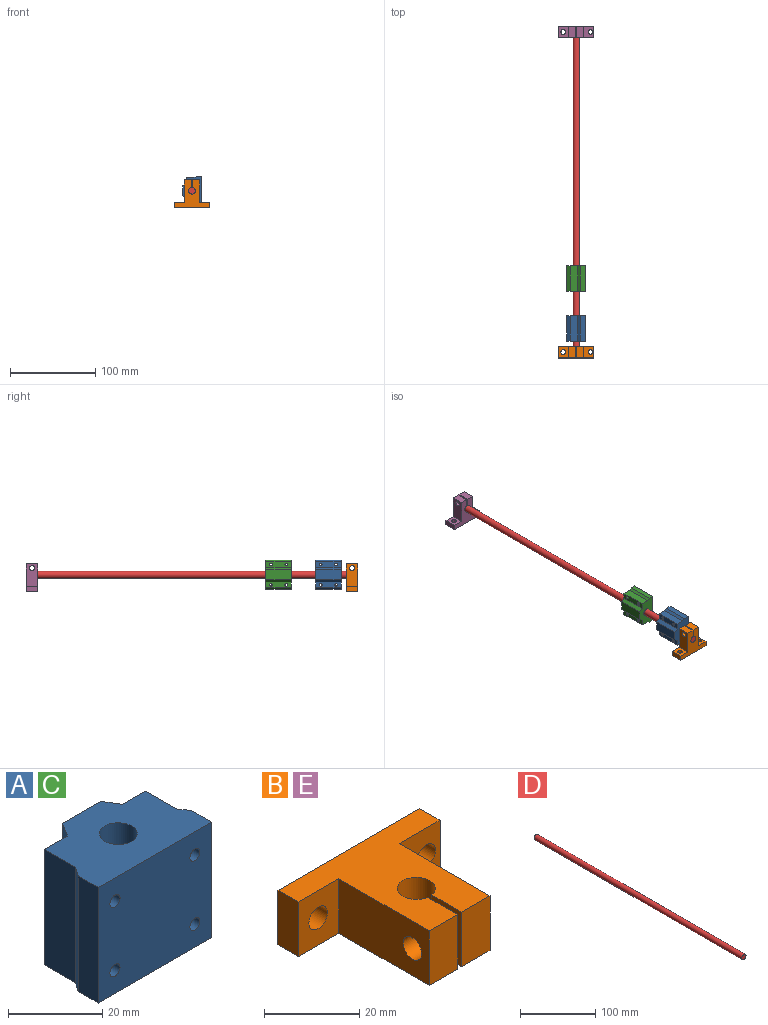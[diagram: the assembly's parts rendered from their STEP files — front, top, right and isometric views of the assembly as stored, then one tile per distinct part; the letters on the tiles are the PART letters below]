
ASSEMBLY  parts=5 mates=4
PART A: 19 faces, bbox 34x22x30 mm
  f0: plane 34x30mm, normal (0,-1,0), area 991mm2, adj f1,f12,f13,f14,f15,f16,f17,f18
  f1: plane 30x6mm, normal (-1,0,0), area 180mm2, adj f0,f2,f13,f14
  f2: plane 30x2.67mm, normal (-0.82,0.57,0), area 97.1mm2, adj f1,f3,f13,f14
  f3: plane 30x9.33mm, normal (-1,0,0), area 280mm2, adj f2,f4,f13,f14
  f4: plane 30x6.93mm, normal (0,1,0), area 193.5mm2, adj f3,f5,f13,f14,f15,f16
  f5: plane 30x4mm, normal (-0.85,0.53,0), area 141.3mm2, adj f4,f6,f13,f14
  f6: plane 30x11.5mm, normal (0,1,0), area 344.9mm2, adj f5,f7,f13,f14
  f7: plane 30x4mm, normal (0.85,0.53,0), area 141.3mm2, adj f6,f8,f13,f14
  f8: plane 30x6.93mm, normal (0,1,0), area 193.5mm2, adj f7,f9,f13,f14,f17,f18
  f9: plane 30x9.33mm, normal (1,0,0), area 280mm2, adj f8,f10,f13,f14
  f10: plane 30x2.67mm, normal (0.82,0.57,0), area 97.1mm2, adj f9,f12,f13,f14
  f11: cylinder r=4mm len=30mm, axis (0,0,-1), area 754mm2, adj f13,f14
  f12: plane 30x6mm, normal (1,0,0), area 180mm2, adj f0,f10,f13,f14
  f13: plane 34x22mm, normal (0,0,1), area 578.6mm2, adj f0,f1,f2,f3,f4,f5,f6,f7
  f14: plane 34x22mm, normal (0,0,-1), area 578.6mm2, adj f0,f1,f2,f3,f4,f5,f6,f7
  f15: cylinder r=1.52mm len=18mm, axis (0,1,0), area 171.9mm2, adj f0,f4
  f16: cylinder r=1.52mm len=18mm, axis (0,1,0), area 171.9mm2, adj f0,f4
  f17: cylinder r=1.52mm len=18mm, axis (0,1,0), area 171.9mm2, adj f0,f8
  f18: cylinder r=1.52mm len=18mm, axis (0,1,0), area 171.9mm2, adj f0,f8
PART B: 18 faces, bbox 42x32.8x14 mm
  f0: plane 42x14mm, normal (0,1,0), area 540.5mm2, adj f1,f11,f12,f13,f14,f15
  f1: plane 14x6mm, normal (1,0,0), area 84mm2, adj f0,f2,f12,f13
  f2: plane 14x12mm, normal (0,-1,0), area 144.2mm2, adj f1,f3,f12,f13,f15
  f3: plane 26.8x14mm, normal (1,0,0), area 351.4mm2, adj f2,f4,f12,f13,f16
  f4: plane 14x8.4mm, normal (0,-1,0), area 117.6mm2, adj f3,f5,f12,f13
  f5: plane 14x8.85mm, normal (-1,0,0), area 100.1mm2, adj f4,f6,f12,f13,f16
  f6: cylinder r=4mm len=14mm, axis (0,0,1), area 335mm2, adj f5,f7,f12,f13
  f7: plane 14x8.85mm, normal (1,0,0), area 100.1mm2, adj f6,f8,f12,f13,f17
  f8: plane 14x8.4mm, normal (0,-1,0), area 117.6mm2, adj f7,f9,f12,f13
  f9: plane 26.8x14mm, normal (-1,0,0), area 351.4mm2, adj f8,f10,f12,f13,f17
  f10: plane 14x12mm, normal (0,-1,0), area 144.2mm2, adj f9,f11,f12,f13,f14
  f11: plane 14x6mm, normal (-1,0,0), area 84mm2, adj f0,f10,f12,f13
  f12: plane 42x32.8mm, normal (0,0,-1), area 673.6mm2, adj f0,f1,f2,f3,f4,f5,f6,f7
  f13: plane 42x32.8mm, normal (0,0,1), area 673.6mm2, adj f0,f1,f2,f3,f4,f5,f6,f7
  f14: cylinder r=2.75mm len=6mm, axis (0,-1,0), area 103.7mm2, adj f0,f10
  f15: cylinder r=2.75mm len=6mm, axis (0,-1,0), area 103.7mm2, adj f0,f2
  f16: cylinder r=2.75mm len=8.4mm, axis (1,0,0), area 145.1mm2, adj f3,f5
  f17: cylinder r=2.75mm len=8.4mm, axis (-1,0,0), area 145.1mm2, adj f7,f9
PART C: same geometry as A
PART D: 3 faces, bbox 8x390x8 mm
  f0: cylinder r=4mm len=390mm, axis (0,-1,0), area 9801.8mm2, adj f1,f2
  f1: plane 8x8mm, normal (0,1,0), area 50.3mm2, adj f0
  f2: plane 8x8mm, normal (0,-1,0), area 50.3mm2, adj f0
PART E: same geometry as B
PLACE A rot(axis=(-0.58,0.58,0.58),120deg) t=(-128.21,-71.32,-77.25)mm
PLACE B rot(axis=(-1,0,0),90deg) t=(-44.51,-77.07,-79.25)mm
PLACE C rot(axis=(-0.58,0.58,0.58),120deg) t=(-128.21,-12.8,-77.25)mm
PLACE D t=(-37.38,-91.07,-89.19)mm
PLACE E rot(axis=(-1,0,0),90deg) t=(-44.51,298.93,-79.25)mm
MATE slider D.f0 <-> A.f11  axis (0,-1,0) through (-90,-76.07,-41.57)mm
MATE fastened D.f0 <-> B.f6  axis (0,-1,0) through (-90,-91.07,-41.57)mm
MATE fastened D.f0 <-> E.f6  axis (0,-1,0) through (-90,298.93,-41.57)mm
MATE slider D.f0 <-> C.f11  axis (0,-1,0) through (-90,-36.07,-41.57)mm
